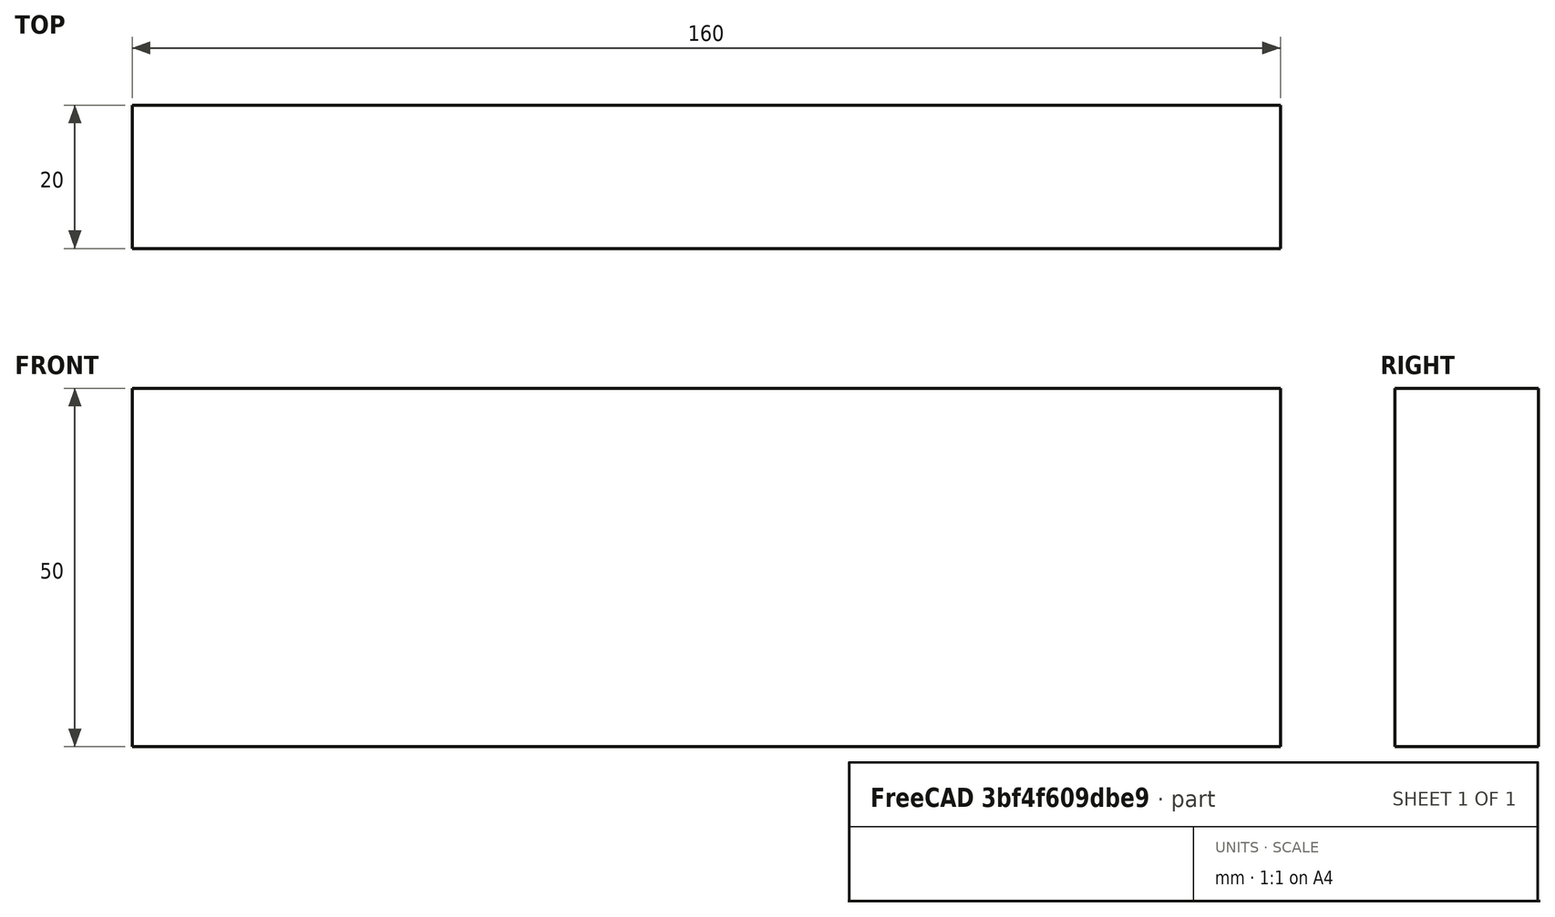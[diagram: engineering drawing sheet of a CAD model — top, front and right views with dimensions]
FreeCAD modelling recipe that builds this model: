
FCSTD DOCUMENT  (FreeCAD 0.15R4671 (Git))
Label: Flat Bar 160x20 EN10058 S235JR
License: All rights reserved
LicenseURL: http://en.wikipedia.org/wiki/All_rights_reserved
objects: Sketcher::SketchObject×1, Part::Extrusion×1
note: 2 computed .brp shape members not serialized (recipe doc carries the construction recipe); baked Part::Feature solids carry a one-line shape summary decoded from their .brp

FEATURE [Sketcher::SketchObject] Sketch
  sketch-geometry (4):
    g0: LineSegment StartX=-80 StartY=-10 StartZ=0 EndX=80 EndY=-10 EndZ=0
    g1: LineSegment StartX=80 StartY=-10 StartZ=0 EndX=80 EndY=10 EndZ=0
    g2: LineSegment StartX=80 StartY=10 StartZ=0 EndX=-80 EndY=10 EndZ=0
    g3: LineSegment StartX=-80 StartY=10 StartZ=0 EndX=-80 EndY=-10 EndZ=0
  constraints (12):
    c: Coincident(g0,g1)
    c: Coincident(g1,g2)
    c: Coincident(g2,g3)
    c: Coincident(g3,g0)
    c: Horizontal(g0)
    c: Horizontal(g2)
    c: Vertical(g1)
    c: Vertical(g3)
    c: Symmetric(g1,g2,g-2)
    c: Symmetric(g0,g1,g-1)
    c: DistanceY(g1) = 20
    c: DistanceX(g0) = 160
FEATURE [Part::Extrusion] Extrude  label="Flat Bar 160x20 EN10058 S235JR"
  Base = -> Sketch
  Dir = (0,0,50)
  Solid = true
